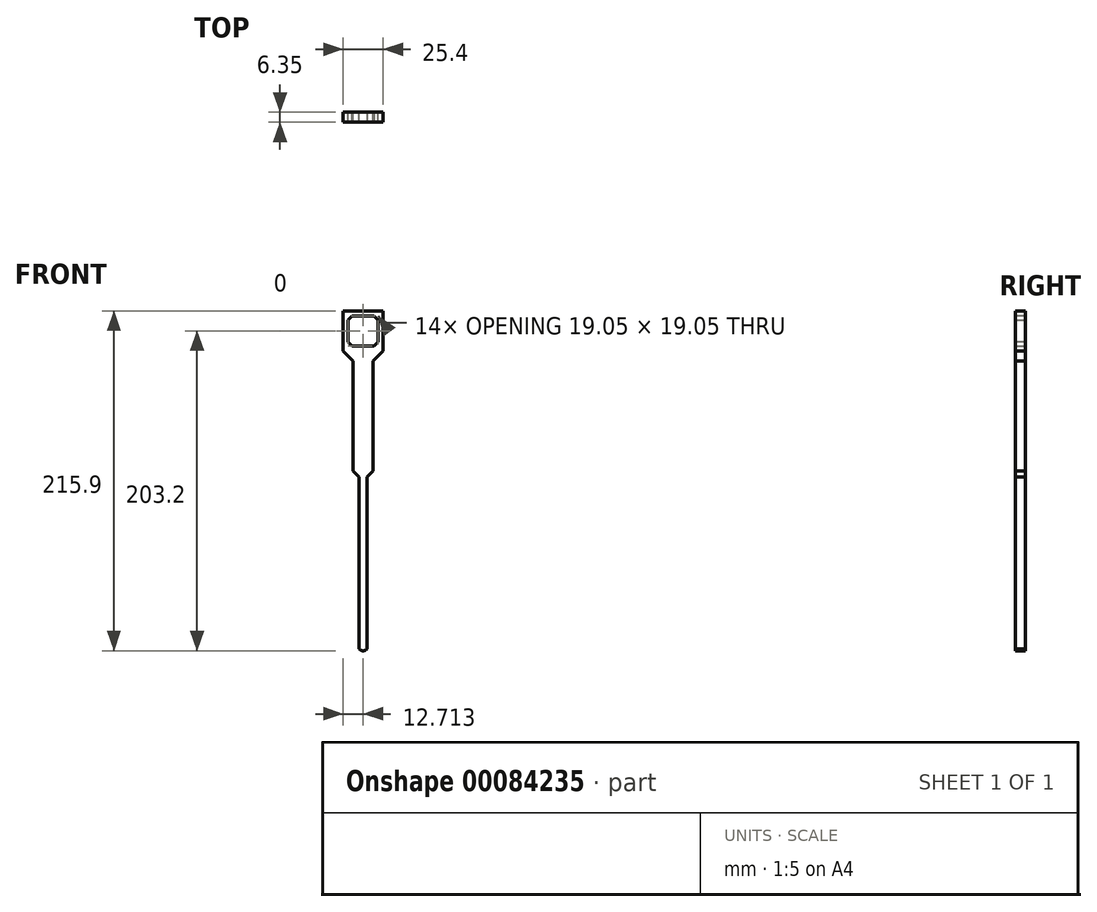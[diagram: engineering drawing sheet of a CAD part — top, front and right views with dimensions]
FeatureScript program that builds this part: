
annotation { "Feature Type Name" : "Feature", "Feature Type Description" : "" }
export const myFeature = defineFeature(function(context is Context, id is Id, definition is map)
    precondition{}
    {
        {
            var Q0;
            Q0=qCreatedBy(makeId("Front.planeOp"),FACE);
            var sketch = newSketch(context, id + "F0", { "sketchPlane" : qUnion([Q0])});
            skLineSegment(sketch, "E0.bottom", {"start": v(12.7, 63.5) * mm, "end": v(-12.7, 63.5) * mm});
            skPoint(sketch, "E0.middle", {"position": v(0, 0) * mm});
            skLineSegment(sketch, "E1.bottom", {"start": v(9.54, 60.33) * mm, "end": v(-9.51, 60.33) * mm});
            skLineSegment(sketch, "E1.left", {"start": v(9.54, 60.33) * mm, "end": v(9.54, 41.28) * mm});
            skLineSegment(sketch, "E1.right", {"start": v(-9.51, 60.33) * mm, "end": v(-9.51, 41.28) * mm});
            skPoint(sketch, "E1.middle", {"position": v(0.01, 50.8) * mm});
            skLineSegment(sketch, "E2", {"start": v(-6.34, 41.28) * mm, "end": v(-9.51, 41.28) * mm});
            skLineSegment(sketch, "E3", {"start": v(6.36, 41.28) * mm, "end": v(9.54, 41.28) * mm});
            skLineSegment(sketch, "E4", {"start": v(-6.34, 38.1) * mm, "end": v(-12.7, 38.1) * mm});
            skLineSegment(sketch, "E5", {"start": v(-12.7, 38.1) * mm, "end": v(-12.7, 63.5) * mm});
            skLineSegment(sketch, "E6", {"start": v(6.36, 38.1) * mm, "end": v(12.7, 38.1) * mm});
            skLineSegment(sketch, "E7", {"start": v(12.7, 63.5) * mm, "end": v(12.7, 38.1) * mm});
            skLineSegment(sketch, "E8", {"start": v(-6.34, 41.28) * mm, "end": v(6.36, 41.28) * mm});
            skPoint(sketch, "E9", {"position": v(6.36, -38.1) * mm});
            skPoint(sketch, "E10", {"position": v(-6.34, -38.1) * mm});
            skLineSegment(sketch, "E11.left", {"start": v(2.54, -38.1) * mm, "end": v(2.54, -38.1) * mm});
            skLineSegment(sketch, "E11.right", {"start": v(-2.54, -38.1) * mm, "end": v(-2.54, -38.1) * mm});
            skPoint(sketch, "E11.middle", {"position": v(0, -38.1) * mm});
            skLineSegment(sketch, "E12", {"start": v(-2.54, -38.1) * mm, "end": v(-2.54, -152.4) * mm});
            skPoint(sketch, "E12.endSnap0", {"position": v(0.01, -152.4) * mm});
            skLineSegment(sketch, "E13", {"start": v(2.54, -38.1) * mm, "end": v(2.54, -152.4) * mm});
            skLineSegment(sketch, "E14", {"start": v(6.36, -38.1) * mm, "end": v(6.36, 38.1) * mm});
            skLineSegment(sketch, "E15", {"start": v(-6.34, -38.1) * mm, "end": v(-6.34, 38.1) * mm});
            skLineSegment(sketch, "E16", {"start": v(-2.54, -152.4) * mm, "end": v(2.54, -152.4) * mm});
            skLineSegment(sketch, "E17", {"start": v(-6.34, -38.1) * mm, "end": v(-2.54, -38.1) * mm});
            skLineSegment(sketch, "E18", {"start": v(2.54, -38.1) * mm, "end": v(6.36, -38.1) * mm});
            skLineSegment(sketch, "E19", {"start": v(-2.54, -38.1) * mm, "end": v(2.54, -38.1) * mm});
            skSolve(sketch);
        }
        {
            var Q0;
            Q0 = qSketchRegion(id + "F0", true);
            extrude(context, id + "F1", {"entities" : qUnion([Q0]), "depth" : 6.35 * mm});
        }
        {
            var Q0;
            Q0=makeQuery(id+"F1.opExtrude","SWEPT_EDGE",EDGE,{"disambiguationData":[OSD([sQuery(id+"F0.wireOp",EDGE,"E12"),sQuery(id+"F0.wireOp",EDGE,"E16")])]});
            var Q1;
            Q1=makeQuery(id+"F1.opExtrude","SWEPT_EDGE",EDGE,{"disambiguationData":[OSD([sQuery(id+"F0.wireOp",EDGE,"E13"),sQuery(id+"F0.wireOp",EDGE,"E16")])]});
            chamfer(context, id + "F2", {"entities" : qUnion([Q0, Q1]), "width" : 1.27 * mm, "tangentPropagation" : true});
        }
        {
            var Q0;
            {var subQ0=sQuery(id+"F0.wireOp",EDGE,"E16");Q0=makeQuery(id+"F2.opChamfer","BLEND_EDGE",EDGE,{"blendedFrom":[makeQuery(id+"F1.opExtrude","SWEPT_EDGE",EDGE,{"disambiguationData":[OSD([sQuery(id+"F0.wireOp",EDGE,"E12"),subQ0])]}),makeQuery(id+"F1.opExtrude","SWEPT_FACE",FACE,{"disambiguationData":[OSD([subQ0])]})],"blendedInto":[makeQuery(id+"F1.opExtrude","SWEPT_FACE",FACE,{"disambiguationData":[OSD([subQ0])]})]});}
            var Q1;
            {var subQ0=sQuery(id+"F0.wireOp",EDGE,"E16");Q1=makeQuery(id+"F2.opChamfer","BLEND_EDGE",EDGE,{"blendedFrom":[makeQuery(id+"F1.opExtrude","SWEPT_EDGE",EDGE,{"disambiguationData":[OSD([sQuery(id+"F0.wireOp",EDGE,"E13"),subQ0])]}),makeQuery(id+"F1.opExtrude","SWEPT_FACE",FACE,{"disambiguationData":[OSD([subQ0])]})],"blendedInto":[makeQuery(id+"F1.opExtrude","SWEPT_FACE",FACE,{"disambiguationData":[OSD([subQ0])]})]});}
            fillet(context, id + "F3", {"entities" : qUnion([Q0, Q1]), "radius" : 2.54 * mm, "tangentPropagation" : true, "allowEdgeOverflow" : false});
        }
        {
            var Q0;
            Q0=makeQuery(id+"F1.opExtrude","SWEPT_EDGE",EDGE,{"disambiguationData":[OSD([sQuery(id+"F0.wireOp",EDGE,"E13"),sQuery(id+"F0.wireOp",EDGE,"E18"),sQuery(id+"F0.wireOp",EDGE,"E19")])]});
            var Q1;
            Q1=makeQuery(id+"F1.opExtrude","SWEPT_EDGE",EDGE,{"disambiguationData":[OSD([sQuery(id+"F0.wireOp",EDGE,"E12"),sQuery(id+"F0.wireOp",EDGE,"E17"),sQuery(id+"F0.wireOp",EDGE,"E19")])]});
            chamfer(context, id + "F4", {"entities" : qUnion([Q0, Q1]), "width" : 3.8 * mm, "tangentPropagation" : true});
        }
        {
            var Q0;
            Q0=makeQuery(id+"F1.opExtrude","SWEPT_EDGE",EDGE,{"disambiguationData":[OSD([sQuery(id+"F0.wireOp",EDGE,"E1.bottom"),sQuery(id+"F0.wireOp",EDGE,"E1.right")])]});
            var Q1;
            Q1=makeQuery(id+"F1.opExtrude","SWEPT_EDGE",EDGE,{"disambiguationData":[OSD([sQuery(id+"F0.wireOp",EDGE,"E1.bottom"),sQuery(id+"F0.wireOp",EDGE,"E1.left")])]});
            var Q2;
            Q2=makeQuery(id+"F1.opExtrude","SWEPT_EDGE",EDGE,{"disambiguationData":[OSD([sQuery(id+"F0.wireOp",EDGE,"E1.right"),sQuery(id+"F0.wireOp",EDGE,"E2")])]});
            var Q3;
            Q3=makeQuery(id+"F1.opExtrude","SWEPT_EDGE",EDGE,{"disambiguationData":[OSD([sQuery(id+"F0.wireOp",EDGE,"E1.left"),sQuery(id+"F0.wireOp",EDGE,"E3")])]});
            chamfer(context, id + "F5", {"entities" : qUnion([Q0, Q1, Q2, Q3]), "width" : 2.54 * mm, "tangentPropagation" : true});
        }
        {
            var Q0;
            Q0=makeQuery(id+"F1.opExtrude","SWEPT_EDGE",EDGE,{"disambiguationData":[OSD([sQuery(id+"F0.wireOp",EDGE,"E6"),sQuery(id+"F0.wireOp",EDGE,"E14")])]});
            var Q1;
            Q1=makeQuery(id+"F1.opExtrude","SWEPT_EDGE",EDGE,{"disambiguationData":[OSD([sQuery(id+"F0.wireOp",EDGE,"E4"),sQuery(id+"F0.wireOp",EDGE,"E15")])]});
            chamfer(context, id + "F6", {"entities" : qUnion([Q0, Q1]), "width" : 6.35 * mm, "tangentPropagation" : true});
        }
    });
